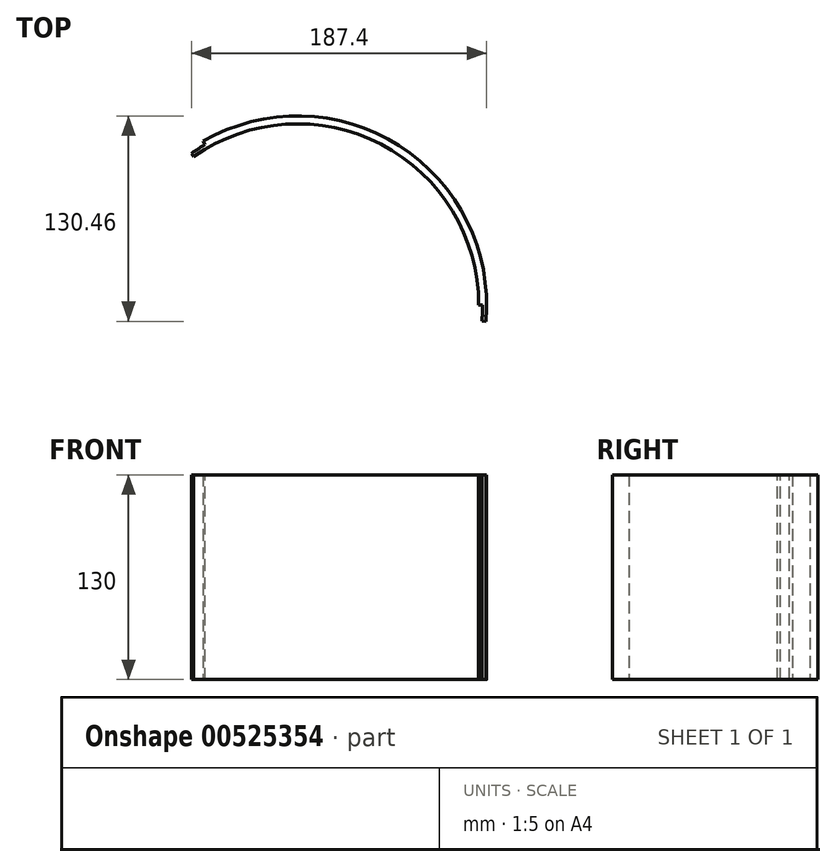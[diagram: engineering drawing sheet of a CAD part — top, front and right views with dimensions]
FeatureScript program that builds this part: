
annotation { "Feature Type Name" : "Feature", "Feature Type Description" : "" }
export const myFeature = defineFeature(function(context is Context, id is Id, definition is map)
    precondition{}
    {
        {
            var Q0;
            Q0=qCreatedBy(makeId("Top.planeOp"),FACE);
            var sketch = newSketch(context, id + "F0", { "sketchPlane" : qUnion([Q0])});
            skArc(sketch, "E0", {"start": v(115, 0) * mm, "mid": v(57.5, 99.6) * mm, "end": v(-57.5, 99.6) * mm});
            skLineSegment(sketch, "E1", {"start": v(115, 0) * mm, "end": v(120, 0) * mm});
            skArc(sketch, "E2", {"start": v(-60, 103.92) * mm, "mid": v(60, 103.92) * mm, "end": v(120, 0) * mm});
            skLineSegment(sketch, "E3", {"start": v(-60, 103.92) * mm, "end": v(-57.5, 99.6) * mm});
            skLineSegment(sketch, "E4", {"start": v(-57.5, 99.6) * mm, "end": v(0, 0) * mm});
            skLineSegment(sketch, "E5", {"start": v(0, 0) * mm, "end": v(115, 0) * mm});
            skSolve(sketch);
        }
        {
            var Q0;
            Q0=makeQuery(id+"F0.imprint","IMPRINT",FACE,{"disambiguationData":[TD([[makeQuery(id+"F0.imprint","IMPRINT",EDGE,{"derivedFrom":sQuery(id+"F0.wireOp",EDGE,"E0")}),-1.0]])]});
            extrude(context, id + "F1", {"entities" : qUnion([Q0]), "depth" : 130 * mm, "offsetDistance" : 25 * mm});
        }
        {
            var Q0;
            Q0=makeQuery(id+"F1.opExtrude","CAP_FACE",FACE,{"disambiguationData":[OSD([sQuery(id+"F0.wireOp",EDGE,"E0"),sQuery(id+"F0.wireOp",EDGE,"E1"),sQuery(id+"F0.wireOp",EDGE,"E2"),sQuery(id+"F0.wireOp",EDGE,"E3")])],"isStart":false});
            var sketch = newSketch(context, id + "F2", { "sketchPlane" : qUnion([Q0])});
            skArc(sketch, "E6", {"start": v(-57.5, 99.6) * mm, "mid": v(-61.79, 97) * mm, "end": v(-65.96, 94.2) * mm});
            skArc(sketch, "E7", {"start": v(-58.75, 101.76) * mm, "mid": v(-63.13, 99.1) * mm, "end": v(-67.4, 96.25) * mm});
            skArc(sketch, "E8", {"start": v(117.5, 0) * mm, "mid": v(117.39, -5.13) * mm, "end": v(117.05, -10.24) * mm});
            skArc(sketch, "E9", {"start": v(120, 0) * mm, "mid": v(119.89, -5.23) * mm, "end": v(119.54, -10.46) * mm});
            skLineSegment(sketch, "E10", {"start": v(-67.4, 96.25) * mm, "end": v(0, 0) * mm});
            skLineSegment(sketch, "E11", {"start": v(119.54, -10.46) * mm, "end": v(0, 0) * mm});
            skLineSegment(sketch, "E12", {"start": v(-58.75, 101.76) * mm, "end": v(-57.5, 99.6) * mm});
            skLineSegment(sketch, "E13", {"start": v(120, 0) * mm, "end": v(117.5, 0) * mm});
            skLineSegment(sketch, "E14", {"start": v(0, 0) * mm, "end": v(60, 103.92) * mm});
            skSolve(sketch);
        }
        {
            var Q0;
            Q0 = qSketchRegion(id + "F2", true);
            extrude(context, id + "F3", {"entities" : qUnion([Q0]), "operationType" : NewBodyOperationType.ADD, "oppositeDirection" : true, "depth" : 130 * mm, "offsetDistance" : 25 * mm});
        }
    });
